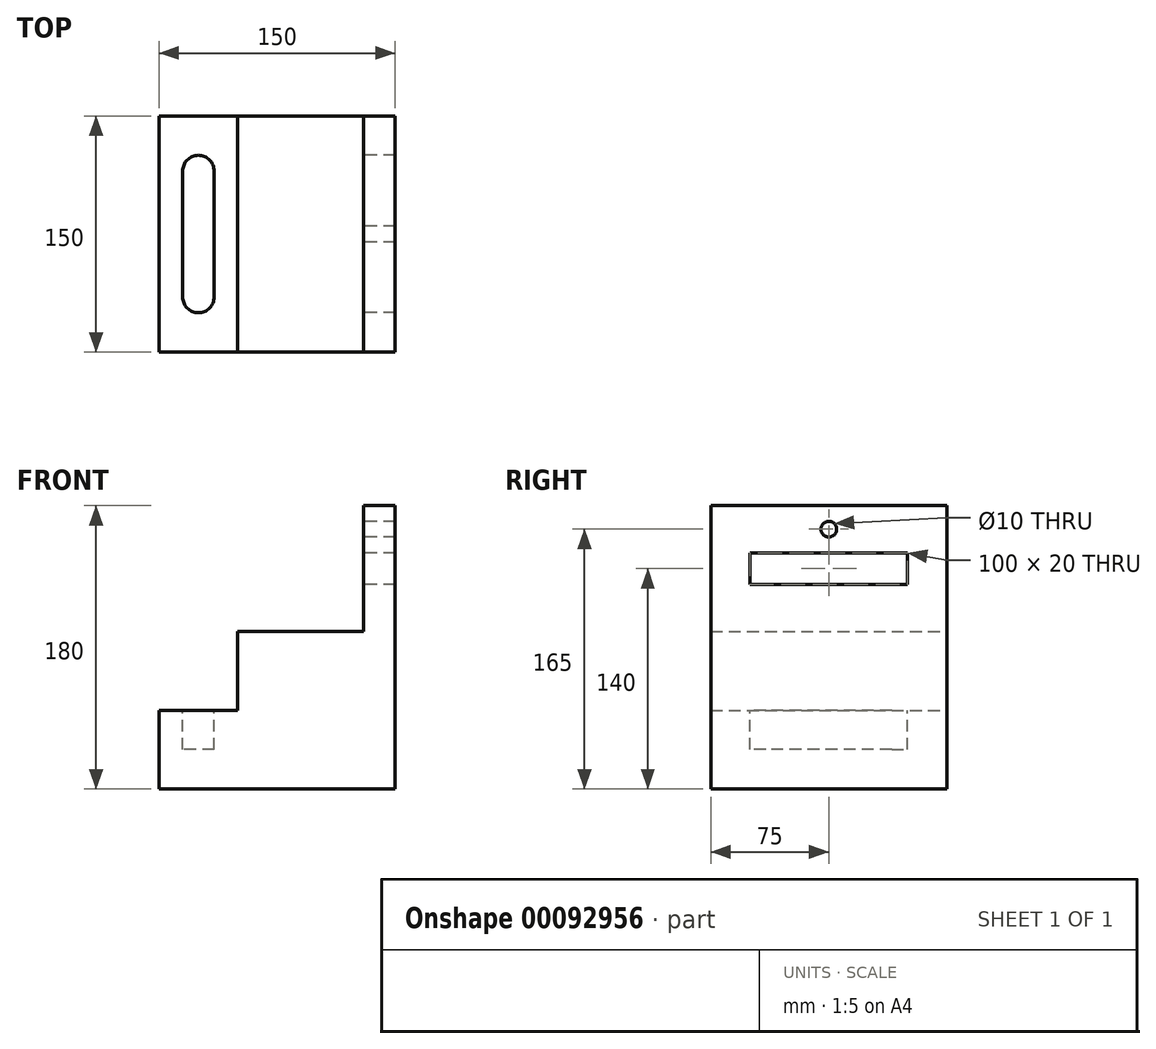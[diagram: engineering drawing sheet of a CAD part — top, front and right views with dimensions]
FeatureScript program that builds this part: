
annotation { "Feature Type Name" : "Feature", "Feature Type Description" : "" }
export const myFeature = defineFeature(function(context is Context, id is Id, definition is map)
    precondition{}
    {
        {
            var Q0;
            Q0=qCreatedBy(makeId("Front.planeOp"),FACE);
            var sketch = newSketch(context, id + "F0", { "sketchPlane" : qUnion([Q0])});
            skLineSegment(sketch, "E0.bottom", {"start": v(75, 25) * mm, "end": v(-75, 25) * mm});
            skLineSegment(sketch, "E0.top", {"start": v(75, -25) * mm, "end": v(-75, -25) * mm});
            skLineSegment(sketch, "E0.left", {"start": v(75, 25) * mm, "end": v(75, -25) * mm});
            skLineSegment(sketch, "E0.right", {"start": v(-75, 25) * mm, "end": v(-75, -25) * mm});
            skPoint(sketch, "E0.middle", {"position": v(0, 0) * mm});
            skLineSegment(sketch, "E1.bottom", {"start": v(75, 25) * mm, "end": v(-25, 25) * mm});
            skLineSegment(sketch, "E1.top", {"start": v(75, 75) * mm, "end": v(-25, 75) * mm});
            skLineSegment(sketch, "E1.left", {"start": v(75, 25) * mm, "end": v(75, 75) * mm});
            skLineSegment(sketch, "E1.right", {"start": v(-25, 25) * mm, "end": v(-25, 75) * mm});
            skLineSegment(sketch, "E2.bottom", {"start": v(75, 75) * mm, "end": v(55, 75) * mm});
            skLineSegment(sketch, "E2.top", {"start": v(75, 155) * mm, "end": v(55, 155) * mm});
            skLineSegment(sketch, "E2.left", {"start": v(75, 75) * mm, "end": v(75, 155) * mm});
            skLineSegment(sketch, "E2.right", {"start": v(55, 75) * mm, "end": v(55, 155) * mm});
            skSolve(sketch);
        }
        {
            var Q0;
            Q0 = qSketchRegion(id + "F0", true);
            extrude(context, id + "F1", {"entities" : qUnion([Q0]), "endBound" : BoundingType.SYMMETRIC, "depth" : 150 * mm});
        }
        {
            var Q0;
            Q0=makeQuery(id+"F1.opExtrude","SWEPT_FACE",FACE,{"disambiguationData":[OSD([sQuery(id+"F0.wireOp",EDGE,"E2.right")])]});
            var sketch = newSketch(context, id + "F2", { "sketchPlane" : qUnion([Q0])});
            skLineSegment(sketch, "E3.bottom", {"start": v(50, 105) * mm, "end": v(-50, 105) * mm});
            skLineSegment(sketch, "E3.top", {"start": v(50, 125) * mm, "end": v(-50, 125) * mm});
            skLineSegment(sketch, "E3.left", {"start": v(50, 105) * mm, "end": v(50, 125) * mm});
            skLineSegment(sketch, "E3.right", {"start": v(-50, 105) * mm, "end": v(-50, 125) * mm});
            skPoint(sketch, "E3.middle", {"position": v(0, 115) * mm});
            skPoint(sketch, "E3.middle.positionSnap0", {"position": v(75, 115) * mm});
            skPoint(sketch, "E3.centerSnap0", {"position": v(75, 115) * mm});
            skCircle(sketch, "E4", {"center": v(0, 140) * mm, "radius": 5 * mm});
            skSolve(sketch);
        }
        {
            var Q0;
            Q0 = qSketchRegion(id + "F2", true);
            extrude(context, id + "F3", {"entities" : qUnion([Q0]), "operationType" : NewBodyOperationType.REMOVE, "endBound" : BoundingType.THROUGH_ALL, "oppositeDirection" : true, "depth" : 25 * mm});
        }
        {
            var Q0;
            Q0=makeQuery(id+"F1.opExtrude","SWEPT_FACE",FACE,{"disambiguationData":[OSD([sQuery(id+"F0.wireOp",EDGE,"E0.bottom")])]});
            var sketch = newSketch(context, id + "F4", { "sketchPlane" : qUnion([Q0])});
            skLineSegment(sketch, "E5.bottom", {"start": v(-50, 50) * mm, "end": v(-50, 50) * mm});
            skLineSegment(sketch, "E5.top", {"start": v(-50, -50) * mm, "end": v(-50, -50) * mm});
            skLineSegment(sketch, "E5.left", {"start": v(-40, 40) * mm, "end": v(-40, -40) * mm});
            skLineSegment(sketch, "E5.right", {"start": v(-60, 40) * mm, "end": v(-60, -40) * mm});
            skPoint(sketch, "E5.middle", {"position": v(-50, 0) * mm});
            skPoint(sketch, "E5.middle.positionSnap0", {"position": v(-75, 0) * mm});
            skPoint(sketch, "E5.middle.positionSnap1", {"position": v(-50, 75) * mm});
            skPoint(sketch, "E5.centerSnap0", {"position": v(-75, 0) * mm});
            skPoint(sketch, "E5.centerSnap1", {"position": v(-50, 75) * mm});
            skPoint(sketch, "E6.visualSharp", {"position": v(-60, 50) * mm});
            skArc(sketch, "E6.filletArc", {"start": v(-50, 50) * mm, "mid": v(-57.07, 47.07) * mm, "end": v(-60, 40) * mm});
            skPoint(sketch, "E7.visualSharp", {"position": v(-40, 50) * mm});
            skArc(sketch, "E7.filletArc", {"start": v(-40, 40) * mm, "mid": v(-42.93, 47.07) * mm, "end": v(-50, 50) * mm});
            skPoint(sketch, "E8.visualSharp", {"position": v(-60, -50) * mm});
            skArc(sketch, "E8.filletArc", {"start": v(-60, -40) * mm, "mid": v(-57.07, -47.07) * mm, "end": v(-50, -50) * mm});
            skPoint(sketch, "E9.visualSharp", {"position": v(-40, -50) * mm});
            skArc(sketch, "E9.filletArc", {"start": v(-50, -50) * mm, "mid": v(-42.93, -47.07) * mm, "end": v(-40, -40) * mm});
            skSolve(sketch);
        }
        {
            var Q0;
            Q0 = qSketchRegion(id + "F4", true);
            extrude(context, id + "F5", {"entities" : qUnion([Q0]), "operationType" : NewBodyOperationType.REMOVE, "oppositeDirection" : true, "depth" : 25 * mm});
        }
    });
